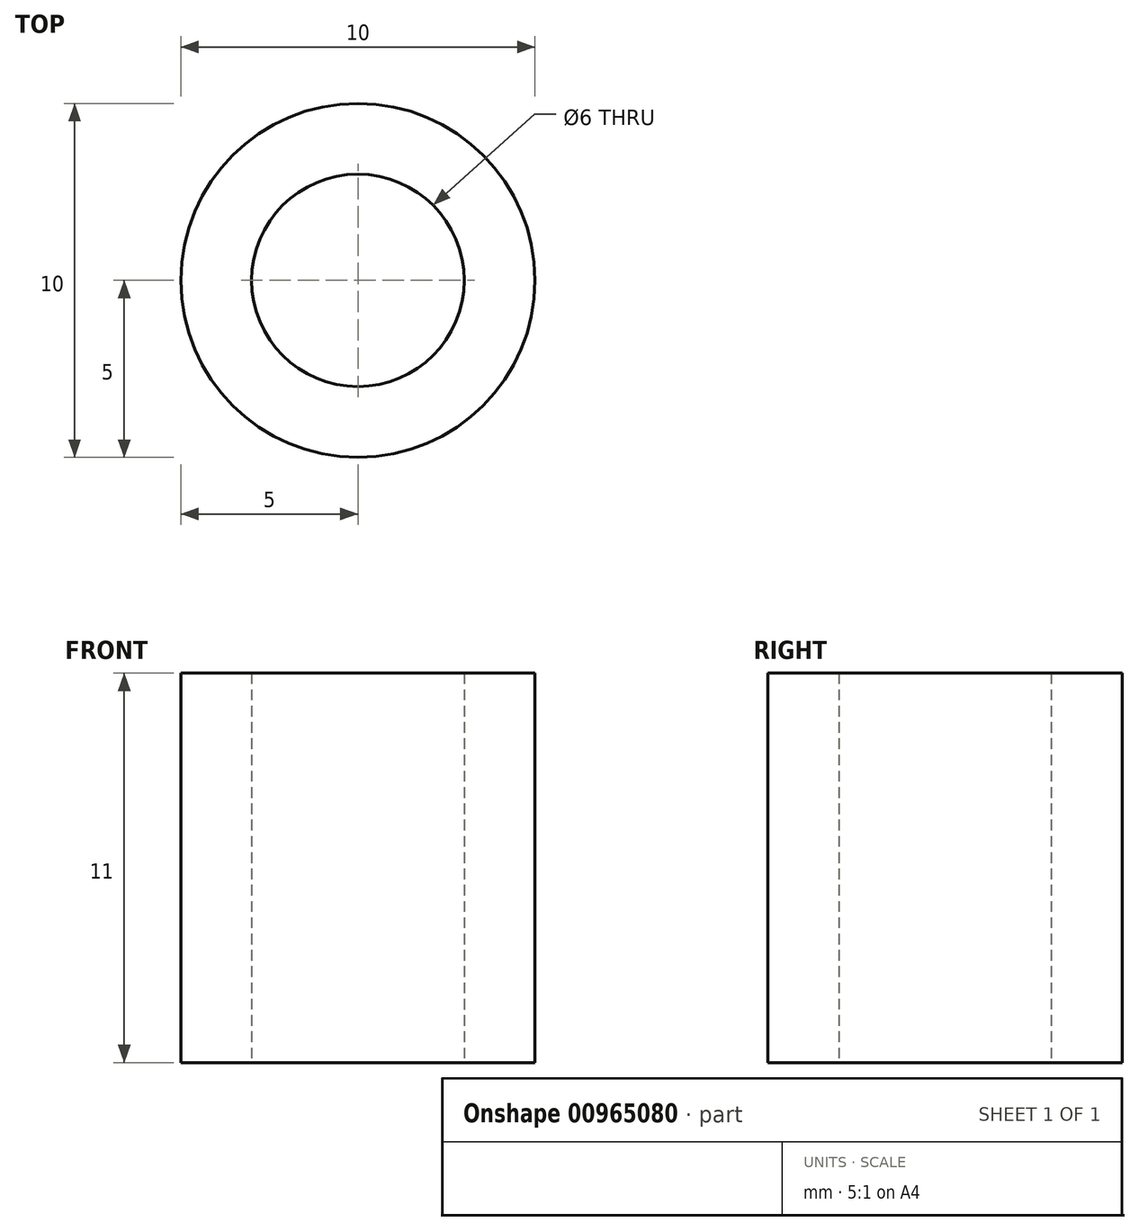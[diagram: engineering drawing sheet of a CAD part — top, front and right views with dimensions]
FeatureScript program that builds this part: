
annotation { "Feature Type Name" : "Feature", "Feature Type Description" : "" }
export const myFeature = defineFeature(function(context is Context, id is Id, definition is map)
    precondition{}
    {
        {
            var Q0;
            Q0=qCreatedBy(makeId("Top.planeOp"),FACE);
            var sketch = newSketch(context, id + "F0", { "sketchPlane" : qUnion([Q0])});
            skCircle(sketch, "E0", {"center": v(0, 0) * mm, "radius": 5 * mm});
            skCircle(sketch, "E1", {"center": v(0, 0) * mm, "radius": 3 * mm});
            skSolve(sketch);
        }
        {
            var Q0;
            Q0=makeQuery(id+"F0.imprint","IMPRINT",FACE,{"disambiguationData":[TD([[makeQuery(id+"F0.imprint","IMPRINT",EDGE,{"derivedFrom":sQuery(id+"F0.wireOp",EDGE,"E0")}),1.0]])]});
            extrude(context, id + "F1", {"entities" : qUnion([Q0]), "depth" : 11 * mm, "offsetDistance" : 25 * mm});
        }
    });
